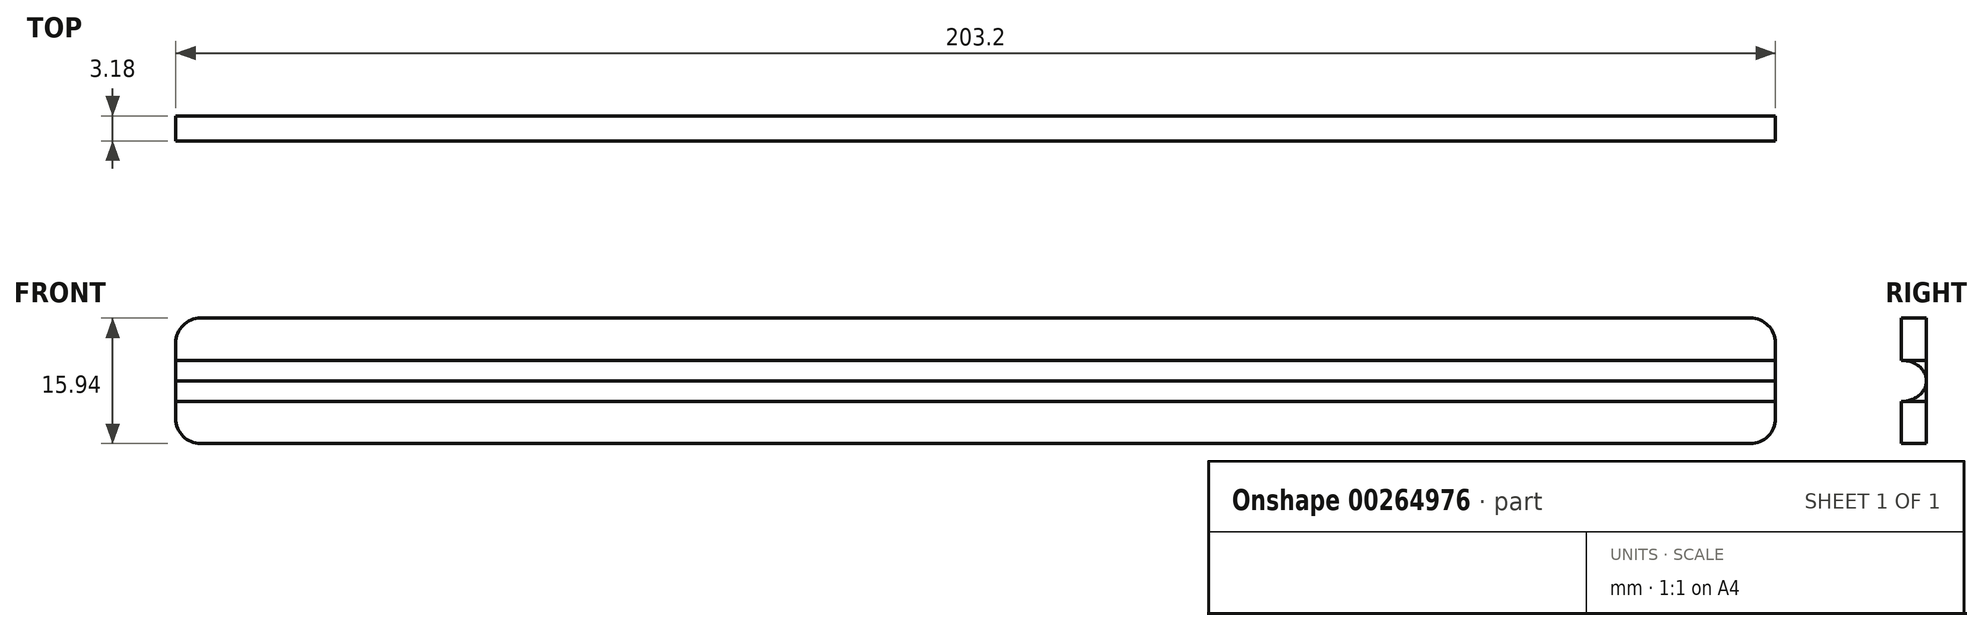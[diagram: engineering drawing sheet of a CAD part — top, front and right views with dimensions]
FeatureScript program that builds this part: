
annotation { "Feature Type Name" : "Feature", "Feature Type Description" : "" }
export const myFeature = defineFeature(function(context is Context, id is Id, definition is map)
    precondition{}
    {
        {
            var Q0;
            Q0=qCreatedBy(makeId("Front.planeOp"),FACE);
            var sketch = newSketch(context, id + "F0", { "sketchPlane" : qUnion([Q0])});
            skLineSegment(sketch, "E0.bottom", {"start": v(-97.84, 8.43) * mm, "end": v(105.36, 8.43) * mm});
            skLineSegment(sketch, "E0.top", {"start": v(-97.84, -7.51) * mm, "end": v(105.36, -7.51) * mm});
            skLineSegment(sketch, "E0.left", {"start": v(-97.84, 8.43) * mm, "end": v(-97.84, -7.51) * mm});
            skLineSegment(sketch, "E0.right", {"start": v(105.36, 8.43) * mm, "end": v(105.36, -7.51) * mm});
            skLineSegment(sketch, "E1.top", {"start": v(-97.84, -2.16) * mm, "end": v(105.36, -2.16) * mm});
            skLineSegment(sketch, "E1.left", {"start": v(-97.84, 0.46) * mm, "end": v(-97.84, -2.16) * mm});
            skLineSegment(sketch, "E1.right", {"start": v(105.36, 0.46) * mm, "end": v(105.36, -2.16) * mm});
            skLineSegment(sketch, "E2.MirrorCS", {"start": v(-97.84, 3.07) * mm, "end": v(105.36, 3.07) * mm});
            skSolve(sketch);
        }
        {
            var Q0;
            {var subQ0=sQuery(id+"F0.wireOp",EDGE,"E0.bottom");Q0=makeQuery(id+"F0.imprint","IMPRINT",FACE,{"disambiguationData":[TD([[makeQuery(id+"F0.imprint","IMPRINT",EDGE,{"derivedFrom":subQ0}),-1.0]])]});}
            var Q1;
            {var subQ0=sQuery(id+"F0.wireOp",EDGE,"E0.top");Q1=makeQuery(id+"F0.imprint","IMPRINT",FACE,{"disambiguationData":[TD([[makeQuery(id+"F0.imprint","IMPRINT",EDGE,{"derivedFrom":subQ0}),1.0]])]});}
            extrude(context, id + "F1", {"entities" : qUnion([Q0, Q1]), "depth" : 3.17 * mm, "offsetDistance" : 25.4 * mm});
        }
        {
            var Q0;
            Q0=makeQuery(id+"F0.imprint","IMPRINT",FACE,{"disambiguationData":[TD([[makeQuery(id+"F0.imprint","IMPRINT",EDGE,{"derivedFrom":sQuery(id+"F0.wireOp",EDGE,"E1.top")}),1.0]])]});
            extrude(context, id + "F2", {"entities" : qUnion([Q0]), "depth" : 3.17 * mm, "offsetDistance" : 25.4 * mm});
        }
        {
            var Q0;
            Q0=makeQuery(id+"F2.opExtrude","SWEPT_FACE",FACE,{"disambiguationData":[OSD([sQuery(id+"F0.wireOp",EDGE,"E0.left"),sQuery(id+"F0.wireOp",EDGE,"E1.left")])]});
            var sketch = newSketch(context, id + "F3", { "sketchPlane" : qUnion([Q0])});
            skFitSpline(sketch, "E3", {"points": [v(3.18, 3.07) * mm, v(0, 0.46) * mm, v(3.18, -2.16) * mm], "startDerivative": vector(-11.37, 0) * mm, "endDerivative": vector(11.37, 0) * mm});
            skSolve(sketch);
        }
        {
            var Q0;
            {var subQ1=sQuery(id+"F0.wireOp",EDGE,"E1.left");var subQ2=sQuery(id+"F0.wireOp",EDGE,"E0.left");var subQ3=makeQuery(id+"F2.opExtrude","CAP_EDGE",EDGE,{"disambiguationData":[OSD([subQ2,subQ1])],"isStart":false});Q0=makeQuery(id+"F3.imprint","IMPRINT",FACE,{"disambiguationData":[TD([[makeQuery(id+"F3.imprint","IMPRINT",EDGE,{"derivedFrom":subQ3}),-1.0]])]});}
            extrude(context, id + "F4", {"entities" : qUnion([Q0]), "operationType" : NewBodyOperationType.REMOVE, "oppositeDirection" : true, "depth" : 203.2 * mm, "offsetDistance" : 25.4 * mm});
        }
        {
            var Q0;
            Q0=makeQuery(id+"F1.opExtrude","SWEPT_EDGE",EDGE,{"disambiguationData":[OSD([sQuery(id+"F0.wireOp",EDGE,"E0.bottom"),sQuery(id+"F0.wireOp",EDGE,"E0.left")])]});
            var Q1;
            Q1=makeQuery(id+"F1.opExtrude","SWEPT_EDGE",EDGE,{"disambiguationData":[OSD([sQuery(id+"F0.wireOp",EDGE,"E0.top"),sQuery(id+"F0.wireOp",EDGE,"E0.left")])]});
            var Q2;
            Q2=makeQuery(id+"F1.opExtrude","SWEPT_EDGE",EDGE,{"disambiguationData":[OSD([sQuery(id+"F0.wireOp",EDGE,"E0.bottom"),sQuery(id+"F0.wireOp",EDGE,"E0.right")])]});
            var Q3;
            Q3=makeQuery(id+"F1.opExtrude","SWEPT_EDGE",EDGE,{"disambiguationData":[OSD([sQuery(id+"F0.wireOp",EDGE,"E0.top"),sQuery(id+"F0.wireOp",EDGE,"E0.right")])]});
            fillet(context, id + "F5", {"entities" : qUnion([Q0, Q1, Q2, Q3]), "radius" : 3.17 * mm, "tangentPropagation" : true, "allowEdgeOverflow" : false});
        }
    });
